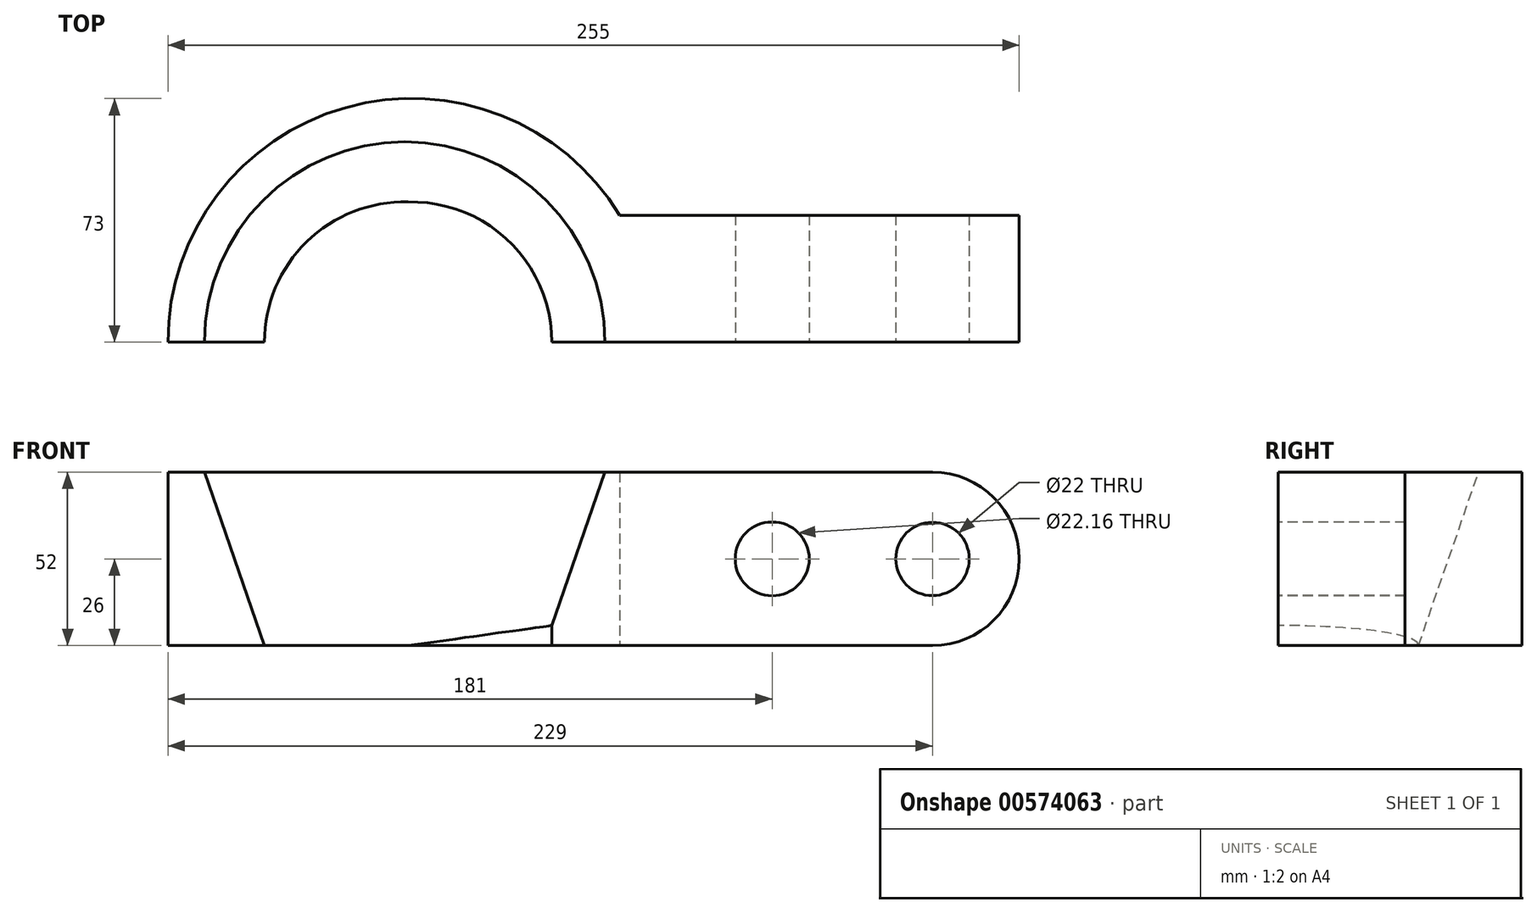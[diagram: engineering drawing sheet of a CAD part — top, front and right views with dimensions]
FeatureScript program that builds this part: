
annotation { "Feature Type Name" : "Feature", "Feature Type Description" : "" }
export const myFeature = defineFeature(function(context is Context, id is Id, definition is map)
    precondition{}
    {
        {
            var Q0;
            Q0=qCreatedBy(makeId("Top.planeOp"),FACE);
            var sketch = newSketch(context, id + "F0", { "sketchPlane" : qUnion([Q0])});
            skArc(sketch, "E0", {"start": v(-10.67, 38) * mm, "mid": v(-92.73, 70.28) * mm, "end": v(-146, 0) * mm});
            skArc(sketch, "E1", {"start": v(-31, 0) * mm, "mid": v(-73, 42) * mm, "end": v(-115, 0) * mm});
            skLineSegment(sketch, "E2", {"start": v(-31, 0) * mm, "end": v(109, 0) * mm});
            skLineSegment(sketch, "E3", {"start": v(109, 0) * mm, "end": v(109, 38) * mm});
            skLineSegment(sketch, "E4", {"start": v(-146, 0) * mm, "end": v(-115, 0) * mm});
            skLineSegment(sketch, "E5", {"start": v(109, 38) * mm, "end": v(-10.67, 38) * mm});
            skSolve(sketch);
        }
        {
            var Q0;
            Q0 = qSketchRegion(id + "F0", true);
            var Q1;
            Q1=makeQuery(id+"F0.imprint","IMPRINT",FACE,{"disambiguationData":[TD([[makeQuery(id+"F0.imprint","IMPRINT",EDGE,{"derivedFrom":sQuery(id+"F0.wireOp",EDGE,"E0")}),1.0]])]});
            extrude(context, id + "F1", {"entities" : qUnion([Q0, Q1]), "depth" : 52 * mm, "offsetDistance" : 25 * mm});
        }
        {
            var Q0;
            Q0=makeQuery(id+"F1.opExtrude","SWEPT_FACE",FACE,{"disambiguationData":[OSD([sQuery(id+"F0.wireOp",EDGE,"E4")])]});
            var sketch = newSketch(context, id + "F2", { "sketchPlane" : qUnion([Q0])});
            skCircle(sketch, "E6", {"center": v(35, 26) * mm, "radius": 11.08 * mm});
            skCircle(sketch, "E7", {"center": v(83, 26) * mm, "radius": 11 * mm});
            skSolve(sketch);
        }
        {
            var Q0;
            Q0=makeQuery(id+"F2.imprint","IMPRINT",FACE,{"disambiguationData":[TD([[makeQuery(id+"F2.imprint","IMPRINT",EDGE,{"derivedFrom":sQuery(id+"F2.wireOp",EDGE,"E6")}),1.0]])]});
            var Q1;
            Q1=makeQuery(id+"F2.imprint","IMPRINT",FACE,{"disambiguationData":[TD([[makeQuery(id+"F2.imprint","IMPRINT",EDGE,{"derivedFrom":sQuery(id+"F2.wireOp",EDGE,"E7")}),1.0]])]});
            extrude(context, id + "F3", {"entities" : qUnion([Q0, Q1]), "operationType" : NewBodyOperationType.REMOVE, "oppositeDirection" : true, "depth" : 51.6 * mm, "offsetDistance" : 25 * mm});
        }
        {
            var Q0;
            Q0=makeQuery(id+"F1.opExtrude","CAP_EDGE",EDGE,{"disambiguationData":[OSD([sQuery(id+"F0.wireOp",EDGE,"E3")])],"isStart":false});
            var Q1;
            Q1=makeQuery(id+"F1.opExtrude","CAP_EDGE",EDGE,{"disambiguationData":[OSD([sQuery(id+"F0.wireOp",EDGE,"E3")])],"isStart":true});
            fillet(context, id + "F4", {"entities" : qUnion([Q0, Q1]), "radius" : 26 * mm, "tangentPropagation" : true, "allowEdgeOverflow" : false});
        }
        {
            var Q0;
            Q0=makeQuery(id+"F1.opExtrude","SWEPT_FACE",FACE,{"disambiguationData":[OSD([sQuery(id+"F0.wireOp",EDGE,"E4")])]});
            var sketch = newSketch(context, id + "F5", { "sketchPlane" : qUnion([Q0])});
            skLineSegment(sketch, "E8", {"start": v(-135.09, 52) * mm, "end": v(-117.09, 0) * mm});
            skLineSegment(sketch, "E9", {"start": v(-117.09, 0) * mm, "end": v(-75.09, 0) * mm});
            skLineSegment(sketch, "E10", {"start": v(-75.09, 0) * mm, "end": v(-75.09, 52) * mm});
            skLineSegment(sketch, "E11", {"start": v(-75.09, 52) * mm, "end": v(-135.09, 52) * mm});
            skSolve(sketch);
        }
        {
            var Q0;
            Q0 = qSketchRegion(id + "F5", true);
            var Q1;
            Q1=sQuery(id+"F5.wireOp",EDGE,"E10");
            revolve(context, id + "F6", {"operationType" : NewBodyOperationType.REMOVE, "entities" : qUnion([Q0]), "axis" : qUnion([Q1]), "revolveType" : RevolveType.FULL, "oppositeDirection" : true});
        }
    });
